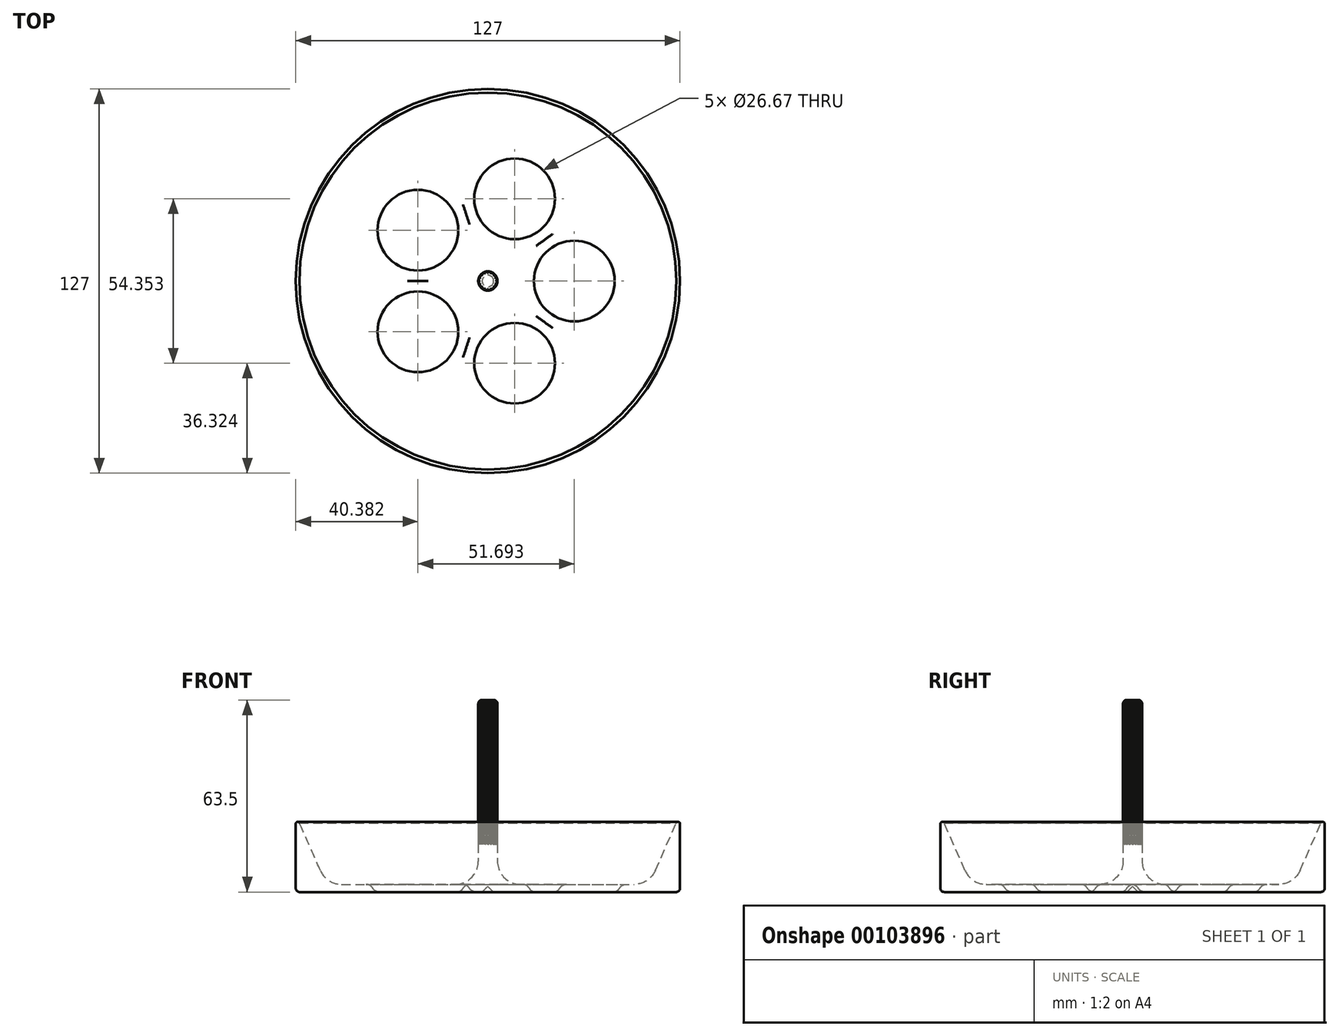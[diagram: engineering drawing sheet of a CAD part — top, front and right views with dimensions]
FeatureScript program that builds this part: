
annotation { "Feature Type Name" : "Feature", "Feature Type Description" : "" }
export const myFeature = defineFeature(function(context is Context, id is Id, definition is map)
    precondition{}
    {
        {
            var Q0;
            Q0=qCreatedBy(makeId("Front.planeOp"),FACE);
            var sketch = newSketch(context, id + "F0", { "sketchPlane" : qUnion([Q0])});
            skLineSegment(sketch, "E0", {"start": v(0, 0) * mm, "end": v(0, 63.5) * mm});
            skLineSegment(sketch, "E1", {"start": v(0, 63.5) * mm, "end": v(1.9, 63.5) * mm});
            skLineSegment(sketch, "E2", {"start": v(63.5, 22.56) * mm, "end": v(63.5, 1.27) * mm});
            skLineSegment(sketch, "E3", {"start": v(1.9, 0) * mm, "end": v(0, 1.9) * mm});
            skPoint(sketch, "E4.visualSharp", {"position": v(3.18, 2.54) * mm});
            skPoint(sketch, "E5.visualSharp", {"position": v(53.34, 2.54) * mm});
            skPoint(sketch, "E6.visualSharp", {"position": v(63.5, 25.4) * mm});
            skArc(sketch, "E6.filletArc", {"start": v(63.5, 22.56) * mm, "mid": v(63, 23.18) * mm, "end": v(62.3, 22.83) * mm});
            skPoint(sketch, "E7", {"position": v(16.72, 2.54) * mm});
            skArc(sketch, "E8", {"start": v(13.62, 1.29) * mm, "mid": v(14.28, 0.54) * mm, "end": v(15.18, 0.1) * mm});
            skArc(sketch, "E9", {"start": v(41.97, 0.1) * mm, "mid": v(42.87, 0.54) * mm, "end": v(43.53, 1.29) * mm});
            skLineSegment(sketch, "E10", {"start": v(62.3, 22.83) * mm, "end": v(55.34, 7.08) * mm});
            skLineSegment(sketch, "E11", {"start": v(3.17, 10.16) * mm, "end": v(3.17, 62.23) * mm});
            skLineSegment(sketch, "E12", {"start": v(10.8, 2.54) * mm, "end": v(11.43, 2.54) * mm});
            skLineSegment(sketch, "E13", {"start": v(45.72, 2.54) * mm, "end": v(48.37, 2.54) * mm});
            skPoint(sketch, "E14.visualSharp", {"position": v(43.9, 2.54) * mm});
            skArc(sketch, "E14.filletArc", {"start": v(45.72, 2.54) * mm, "mid": v(44.46, 2.2) * mm, "end": v(43.53, 1.29) * mm});
            skPoint(sketch, "E15.visualSharp", {"position": v(13.26, 2.54) * mm});
            skArc(sketch, "E15.filletArc", {"start": v(13.62, 1.29) * mm, "mid": v(12.7, 2.2) * mm, "end": v(11.43, 2.54) * mm});
            skLineSegment(sketch, "E16", {"start": v(11.43, 2.54) * mm, "end": v(45.72, 2.54) * mm});
            skLineSegment(sketch, "E17", {"start": v(1.9, 0) * mm, "end": v(15.88, 0) * mm});
            skLineSegment(sketch, "E18", {"start": v(15.88, 0) * mm, "end": v(41.28, 0) * mm});
            skLineSegment(sketch, "E19", {"start": v(41.28, 0) * mm, "end": v(62.23, 0) * mm});
            skLineSegment(sketch, "E20", {"start": v(28.58, 0) * mm, "end": v(28.57, 10.96) * mm});
            skArc(sketch, "E21.filletArc", {"start": v(3.17, 10.16) * mm, "mid": v(5.4, 4.77) * mm, "end": v(10.8, 2.54) * mm});
            skArc(sketch, "E22.filletArc", {"start": v(48.37, 2.54) * mm, "mid": v(52.53, 3.78) * mm, "end": v(55.34, 7.08) * mm});
            skPoint(sketch, "E23.visualSharp", {"position": v(3.17, 63.5) * mm});
            skArc(sketch, "E23.filletArc", {"start": v(3.17, 62.23) * mm, "mid": v(2.8, 63.13) * mm, "end": v(1.9, 63.5) * mm});
            skPoint(sketch, "E24.visualSharp", {"position": v(63.5, 0) * mm});
            skArc(sketch, "E24.filletArc", {"start": v(62.23, 0) * mm, "mid": v(63.13, 0.37) * mm, "end": v(63.5, 1.27) * mm});
            skLineSegment(sketch, "E25", {"start": v(15.24, 0) * mm, "end": v(15.24, 0.01) * mm});
            skLineSegment(sketch, "E26.MirrorCS", {"start": v(41.91, 0) * mm, "end": v(41.91, 0.01) * mm});
            skLineSegment(sketch, "E27.trimOffspring", {"start": v(15.24, 2.54) * mm, "end": v(15.24, 3.63) * mm});
            skLineSegment(sketch, "E28.trimOffspring", {"start": v(41.91, 2.54) * mm, "end": v(41.91, 3.63) * mm});
            skPoint(sketch, "E29.visualSharp", {"position": v(41.91, 0.08) * mm});
            skArc(sketch, "E29.filletArc", {"start": v(41.97, 0.1) * mm, "mid": v(41.93, 0.06) * mm, "end": v(41.91, 0.01) * mm});
            skPoint(sketch, "E30.visualSharp", {"position": v(15.24, 0.08) * mm});
            skArc(sketch, "E30.filletArc", {"start": v(15.24, 0.01) * mm, "mid": v(15.22, 0.06) * mm, "end": v(15.18, 0.1) * mm});
            skSolve(sketch);
        }
        {
            var Q0;
            {var subQ1=sQuery(id+"F0.wireOp",EDGE,"E1");Q0=makeQuery(id+"F0.imprint","IMPRINT",FACE,{"disambiguationData":[TD([[makeQuery(id+"F0.imprint","IMPRINT",EDGE,{"derivedFrom":subQ1}),-1.0]])]});}
            var Q1;
            {var subQ1=sQuery(id+"F0.wireOp",EDGE,"E8");Q1=makeQuery(id+"F0.imprint","IMPRINT",FACE,{"disambiguationData":[TD([[makeQuery(id+"F0.imprint","IMPRINT",EDGE,{"derivedFrom":subQ1}),1.0]])]});}
            var Q2;
            {var subQ1=sQuery(id+"F0.wireOp",EDGE,"E9");Q2=makeQuery(id+"F0.imprint","IMPRINT",FACE,{"disambiguationData":[TD([[makeQuery(id+"F0.imprint","IMPRINT",EDGE,{"derivedFrom":subQ1}),1.0]])]});}
            var Q3;
            Q3=makeQuery(id+"F0.imprint","IMPRINT",FACE,{"disambiguationData":[TD([[makeQuery(id+"F0.imprint","IMPRINT",EDGE,{"derivedFrom":sQuery(id+"F0.wireOp",EDGE,"E2")}),-1.0]])]});
            var Q4;
            Q4=sQuery(id+"F0.wireOp",EDGE,"E0");
            revolve(context, id + "F1", {"entities" : qUnion([Q0, Q1, Q2, Q3]), "axis" : qUnion([Q4]), "revolveType" : RevolveType.FULL});
        }
        {
            var Q0;
            {var subQ1=sQuery(id+"F0.wireOp",EDGE,"E8");Q0=makeQuery(id+"F0.imprint","IMPRINT",FACE,{"disambiguationData":[TD([[makeQuery(id+"F0.imprint","IMPRINT",EDGE,{"derivedFrom":subQ1}),1.0]])]});}
            var Q1;
            Q1=sQuery(id+"F0.wireOp",EDGE,"E20");
            revolve(context, id + "F2", {"entities" : qUnion([Q0]), "axis" : qUnion([Q1]), "revolveType" : RevolveType.FULL});
        }
        {
            var Q0;
            Q0=makeQuery(id+"F2.opRevolve","SWEPT_BODY",BODY,{"disambiguationData":[OSD([sQuery(id+"F0.wireOp",EDGE,"E8"),sQuery(id+"F0.wireOp",EDGE,"E15.filletArc"),sQuery(id+"F0.wireOp",EDGE,"E16"),sQuery(id+"F0.wireOp",EDGE,"E18"),sQuery(id+"F0.wireOp",EDGE,"E20")])]});
            var Q1;
            Q1=sQuery(id+"F0.wireOp",EDGE,"E0");
            circularPattern(context, id + "F3", {"entities" : qUnion([Q0]), "axis" : qUnion([Q1]), "angle" : 360 * degree, "instanceCount" : 5, "equalSpace" : true});
        }
        {
            var Q0;
            Q0=makeQuery(id+"F2.opRevolve","SWEPT_BODY",BODY,{"disambiguationData":[OSD([sQuery(id+"F0.wireOp",EDGE,"E8"),sQuery(id+"F0.wireOp",EDGE,"E15.filletArc"),sQuery(id+"F0.wireOp",EDGE,"E16"),sQuery(id+"F0.wireOp",EDGE,"E18"),sQuery(id+"F0.wireOp",EDGE,"E20")])]});
            var Q1;
            Q1=makeQuery(id+"F3.opPattern","COPY",BODY,{"derivedFrom":makeQuery(id+"F2.opRevolve","SWEPT_BODY",BODY,{"disambiguationData":[OSD([sQuery(id+"F0.wireOp",EDGE,"E8"),sQuery(id+"F0.wireOp",EDGE,"E15.filletArc"),sQuery(id+"F0.wireOp",EDGE,"E16"),sQuery(id+"F0.wireOp",EDGE,"E18"),sQuery(id+"F0.wireOp",EDGE,"E20")])]}),"instanceName":"1"});
            var Q2;
            Q2=makeQuery(id+"F3.opPattern","COPY",BODY,{"derivedFrom":makeQuery(id+"F2.opRevolve","SWEPT_BODY",BODY,{"disambiguationData":[OSD([sQuery(id+"F0.wireOp",EDGE,"E8"),sQuery(id+"F0.wireOp",EDGE,"E15.filletArc"),sQuery(id+"F0.wireOp",EDGE,"E16"),sQuery(id+"F0.wireOp",EDGE,"E18"),sQuery(id+"F0.wireOp",EDGE,"E20")])]}),"instanceName":"2"});
            var Q3;
            Q3=makeQuery(id+"F3.opPattern","COPY",BODY,{"derivedFrom":makeQuery(id+"F2.opRevolve","SWEPT_BODY",BODY,{"disambiguationData":[OSD([sQuery(id+"F0.wireOp",EDGE,"E8"),sQuery(id+"F0.wireOp",EDGE,"E15.filletArc"),sQuery(id+"F0.wireOp",EDGE,"E16"),sQuery(id+"F0.wireOp",EDGE,"E18"),sQuery(id+"F0.wireOp",EDGE,"E20")])]}),"instanceName":"3"});
            var Q4;
            Q4=makeQuery(id+"F3.opPattern","COPY",BODY,{"derivedFrom":makeQuery(id+"F2.opRevolve","SWEPT_BODY",BODY,{"disambiguationData":[OSD([sQuery(id+"F0.wireOp",EDGE,"E8"),sQuery(id+"F0.wireOp",EDGE,"E15.filletArc"),sQuery(id+"F0.wireOp",EDGE,"E16"),sQuery(id+"F0.wireOp",EDGE,"E18"),sQuery(id+"F0.wireOp",EDGE,"E20")])]}),"instanceName":"4"});
            var Q5;
            Q5=makeQuery(id+"F1.opRevolve","SWEPT_BODY",BODY,{"disambiguationData":[OSD([sQuery(id+"F0.wireOp",EDGE,"E0"),sQuery(id+"F0.wireOp",EDGE,"E1"),sQuery(id+"F0.wireOp",EDGE,"E2"),sQuery(id+"F0.wireOp",EDGE,"E3"),sQuery(id+"F0.wireOp",EDGE,"E6.filletArc"),sQuery(id+"F0.wireOp",EDGE,"E10"),sQuery(id+"F0.wireOp",EDGE,"E11"),sQuery(id+"F0.wireOp",EDGE,"E12"),sQuery(id+"F0.wireOp",EDGE,"E13"),sQuery(id+"F0.wireOp",EDGE,"E16"),sQuery(id+"F0.wireOp",EDGE,"E17"),sQuery(id+"F0.wireOp",EDGE,"E18"),sQuery(id+"F0.wireOp",EDGE,"E19"),sQuery(id+"F0.wireOp",EDGE,"E21.filletArc"),sQuery(id+"F0.wireOp",EDGE,"E22.filletArc")])]});
            booleanBodies(context, id + "F4", {"operationType" : BooleanOperationType.SUBTRACTION, "tools" : qUnion([Q0, Q1, Q2, Q3, Q4]), "targets" : qUnion([Q5])});
        }
        {
            var Q0;
            Q0=qCreatedBy(makeId("Top.planeOp"),FACE);
            var sketch = newSketch(context, id + "F5", { "sketchPlane" : qUnion([Q0])});
            skCircle(sketch, "E31", {"center": v(0, 0) * mm, "radius": 3.18 * mm});
            skLineSegment(sketch, "E32", {"start": v(0, 2.66) * mm, "end": v(0.3, 3.16) * mm});
            skLineSegment(sketch, "E33.MirrorCS", {"start": v(0, 2.66) * mm, "end": v(-0.3, 3.16) * mm});
            skLineSegment(sketch, "E34.1.0", {"start": v(-0.82, 2.53) * mm, "end": v(-0.68, 3.1) * mm});
            skLineSegment(sketch, "E34.1.1", {"start": v(-0.82, 2.53) * mm, "end": v(-1.27, 2.9) * mm});
            skLineSegment(sketch, "E34.2.0", {"start": v(-1.57, 2.16) * mm, "end": v(-1.6, 2.74) * mm});
            skLineSegment(sketch, "E34.2.1", {"start": v(-1.57, 2.16) * mm, "end": v(-2.1, 2.37) * mm});
            skLineSegment(sketch, "E34.3.0", {"start": v(-2.16, 1.57) * mm, "end": v(-2.37, 2.1) * mm});
            skLineSegment(sketch, "E34.3.1", {"start": v(-2.16, 1.57) * mm, "end": v(-2.74, 1.6) * mm});
            skLineSegment(sketch, "E34.4.0", {"start": v(-2.53, 0.82) * mm, "end": v(-2.9, 1.27) * mm});
            skLineSegment(sketch, "E34.4.1", {"start": v(-2.53, 0.82) * mm, "end": v(-3.1, 0.68) * mm});
            skLineSegment(sketch, "E34.5.0", {"start": v(-2.66, 0) * mm, "end": v(-3.16, 0.3) * mm});
            skLineSegment(sketch, "E34.5.1", {"start": v(-2.66, 0) * mm, "end": v(-3.16, -0.3) * mm});
            skLineSegment(sketch, "E34.6.0", {"start": v(-2.53, -0.82) * mm, "end": v(-3.1, -0.68) * mm});
            skLineSegment(sketch, "E34.6.1", {"start": v(-2.53, -0.82) * mm, "end": v(-2.9, -1.27) * mm});
            skLineSegment(sketch, "E34.7.0", {"start": v(-2.16, -1.57) * mm, "end": v(-2.74, -1.6) * mm});
            skLineSegment(sketch, "E34.7.1", {"start": v(-2.16, -1.57) * mm, "end": v(-2.37, -2.1) * mm});
            skLineSegment(sketch, "E34.8.0", {"start": v(-1.57, -2.16) * mm, "end": v(-2.1, -2.37) * mm});
            skLineSegment(sketch, "E34.8.1", {"start": v(-1.57, -2.16) * mm, "end": v(-1.6, -2.74) * mm});
            skLineSegment(sketch, "E34.9.0", {"start": v(-0.82, -2.53) * mm, "end": v(-1.27, -2.9) * mm});
            skLineSegment(sketch, "E34.9.1", {"start": v(-0.82, -2.53) * mm, "end": v(-0.68, -3.1) * mm});
            skLineSegment(sketch, "E34.10.0", {"start": v(0, -2.66) * mm, "end": v(-0.3, -3.16) * mm});
            skLineSegment(sketch, "E34.10.1", {"start": v(0, -2.66) * mm, "end": v(0.3, -3.16) * mm});
            skLineSegment(sketch, "E34.11.0", {"start": v(0.82, -2.53) * mm, "end": v(0.68, -3.1) * mm});
            skLineSegment(sketch, "E34.11.1", {"start": v(0.82, -2.53) * mm, "end": v(1.27, -2.9) * mm});
            skLineSegment(sketch, "E34.12.0", {"start": v(1.57, -2.16) * mm, "end": v(1.6, -2.74) * mm});
            skLineSegment(sketch, "E34.12.1", {"start": v(1.57, -2.16) * mm, "end": v(2.1, -2.37) * mm});
            skLineSegment(sketch, "E34.13.0", {"start": v(2.16, -1.57) * mm, "end": v(2.37, -2.1) * mm});
            skLineSegment(sketch, "E34.13.1", {"start": v(2.16, -1.57) * mm, "end": v(2.74, -1.6) * mm});
            skLineSegment(sketch, "E34.14.0", {"start": v(2.53, -0.82) * mm, "end": v(2.9, -1.27) * mm});
            skLineSegment(sketch, "E34.14.1", {"start": v(2.53, -0.82) * mm, "end": v(3.1, -0.68) * mm});
            skLineSegment(sketch, "E34.15.0", {"start": v(2.66, 0) * mm, "end": v(3.16, -0.3) * mm});
            skLineSegment(sketch, "E34.15.1", {"start": v(2.66, 0) * mm, "end": v(3.16, 0.3) * mm});
            skLineSegment(sketch, "E34.16.0", {"start": v(2.53, 0.82) * mm, "end": v(3.1, 0.68) * mm});
            skLineSegment(sketch, "E34.16.1", {"start": v(2.53, 0.82) * mm, "end": v(2.9, 1.27) * mm});
            skLineSegment(sketch, "E34.17.0", {"start": v(2.16, 1.57) * mm, "end": v(2.74, 1.6) * mm});
            skLineSegment(sketch, "E34.17.1", {"start": v(2.16, 1.57) * mm, "end": v(2.37, 2.1) * mm});
            skLineSegment(sketch, "E34.18.0", {"start": v(1.57, 2.16) * mm, "end": v(2.1, 2.37) * mm});
            skLineSegment(sketch, "E34.18.1", {"start": v(1.57, 2.16) * mm, "end": v(1.6, 2.74) * mm});
            skLineSegment(sketch, "E34.19.0", {"start": v(0.82, 2.53) * mm, "end": v(1.27, 2.9) * mm});
            skLineSegment(sketch, "E34.19.1", {"start": v(0.82, 2.53) * mm, "end": v(0.68, 3.1) * mm});
            skSolve(sketch);
        }
        {
            var Q0;
            {var subQ0=sQuery(id+"F5.wireOp",EDGE,"E34.3.0");Q0=makeQuery(id+"F5.imprint","IMPRINT",FACE,{"disambiguationData":[TD([[makeQuery(id+"F5.imprint","IMPRINT",EDGE,{"derivedFrom":subQ0}),1.0]])]});}
            var Q1;
            {var subQ0=sQuery(id+"F5.wireOp",EDGE,"E34.4.0");Q1=makeQuery(id+"F5.imprint","IMPRINT",FACE,{"disambiguationData":[TD([[makeQuery(id+"F5.imprint","IMPRINT",EDGE,{"derivedFrom":subQ0}),1.0]])]});}
            var Q2;
            {var subQ0=sQuery(id+"F5.wireOp",EDGE,"E34.5.0");Q2=makeQuery(id+"F5.imprint","IMPRINT",FACE,{"disambiguationData":[TD([[makeQuery(id+"F5.imprint","IMPRINT",EDGE,{"derivedFrom":subQ0}),1.0]])]});}
            var Q3;
            {var subQ0=sQuery(id+"F5.wireOp",EDGE,"E34.6.0");Q3=makeQuery(id+"F5.imprint","IMPRINT",FACE,{"disambiguationData":[TD([[makeQuery(id+"F5.imprint","IMPRINT",EDGE,{"derivedFrom":subQ0}),1.0]])]});}
            var Q4;
            {var subQ0=sQuery(id+"F5.wireOp",EDGE,"E34.7.0");Q4=makeQuery(id+"F5.imprint","IMPRINT",FACE,{"disambiguationData":[TD([[makeQuery(id+"F5.imprint","IMPRINT",EDGE,{"derivedFrom":subQ0}),1.0]])]});}
            var Q5;
            {var subQ0=sQuery(id+"F5.wireOp",EDGE,"E34.8.0");Q5=makeQuery(id+"F5.imprint","IMPRINT",FACE,{"disambiguationData":[TD([[makeQuery(id+"F5.imprint","IMPRINT",EDGE,{"derivedFrom":subQ0}),1.0]])]});}
            var Q6;
            {var subQ0=sQuery(id+"F5.wireOp",EDGE,"E34.9.0");Q6=makeQuery(id+"F5.imprint","IMPRINT",FACE,{"disambiguationData":[TD([[makeQuery(id+"F5.imprint","IMPRINT",EDGE,{"derivedFrom":subQ0}),1.0]])]});}
            var Q7;
            {var subQ0=sQuery(id+"F5.wireOp",EDGE,"E34.10.0");Q7=makeQuery(id+"F5.imprint","IMPRINT",FACE,{"disambiguationData":[TD([[makeQuery(id+"F5.imprint","IMPRINT",EDGE,{"derivedFrom":subQ0}),1.0]])]});}
            var Q8;
            {var subQ0=sQuery(id+"F5.wireOp",EDGE,"E34.11.0");Q8=makeQuery(id+"F5.imprint","IMPRINT",FACE,{"disambiguationData":[TD([[makeQuery(id+"F5.imprint","IMPRINT",EDGE,{"derivedFrom":subQ0}),1.0]])]});}
            var Q9;
            {var subQ0=sQuery(id+"F5.wireOp",EDGE,"E34.12.0");Q9=makeQuery(id+"F5.imprint","IMPRINT",FACE,{"disambiguationData":[TD([[makeQuery(id+"F5.imprint","IMPRINT",EDGE,{"derivedFrom":subQ0}),1.0]])]});}
            var Q10;
            {var subQ0=sQuery(id+"F5.wireOp",EDGE,"E34.13.0");Q10=makeQuery(id+"F5.imprint","IMPRINT",FACE,{"disambiguationData":[TD([[makeQuery(id+"F5.imprint","IMPRINT",EDGE,{"derivedFrom":subQ0}),1.0]])]});}
            var Q11;
            {var subQ0=sQuery(id+"F5.wireOp",EDGE,"E34.14.0");Q11=makeQuery(id+"F5.imprint","IMPRINT",FACE,{"disambiguationData":[TD([[makeQuery(id+"F5.imprint","IMPRINT",EDGE,{"derivedFrom":subQ0}),1.0]])]});}
            var Q12;
            {var subQ0=sQuery(id+"F5.wireOp",EDGE,"E34.15.0");Q12=makeQuery(id+"F5.imprint","IMPRINT",FACE,{"disambiguationData":[TD([[makeQuery(id+"F5.imprint","IMPRINT",EDGE,{"derivedFrom":subQ0}),1.0]])]});}
            var Q13;
            {var subQ0=sQuery(id+"F5.wireOp",EDGE,"E34.16.0");Q13=makeQuery(id+"F5.imprint","IMPRINT",FACE,{"disambiguationData":[TD([[makeQuery(id+"F5.imprint","IMPRINT",EDGE,{"derivedFrom":subQ0}),1.0]])]});}
            var Q14;
            {var subQ0=sQuery(id+"F5.wireOp",EDGE,"E34.17.0");Q14=makeQuery(id+"F5.imprint","IMPRINT",FACE,{"disambiguationData":[TD([[makeQuery(id+"F5.imprint","IMPRINT",EDGE,{"derivedFrom":subQ0}),1.0]])]});}
            var Q15;
            {var subQ0=sQuery(id+"F5.wireOp",EDGE,"E34.18.0");Q15=makeQuery(id+"F5.imprint","IMPRINT",FACE,{"disambiguationData":[TD([[makeQuery(id+"F5.imprint","IMPRINT",EDGE,{"derivedFrom":subQ0}),1.0]])]});}
            var Q16;
            {var subQ0=sQuery(id+"F5.wireOp",EDGE,"E34.19.0");Q16=makeQuery(id+"F5.imprint","IMPRINT",FACE,{"disambiguationData":[TD([[makeQuery(id+"F5.imprint","IMPRINT",EDGE,{"derivedFrom":subQ0}),1.0]])]});}
            var Q17;
            {var subQ0=sQuery(id+"F5.wireOp",EDGE,"E32");Q17=makeQuery(id+"F5.imprint","IMPRINT",FACE,{"disambiguationData":[TD([[makeQuery(id+"F5.imprint","IMPRINT",EDGE,{"derivedFrom":subQ0}),1.0]])]});}
            var Q18;
            {var subQ0=sQuery(id+"F5.wireOp",EDGE,"E34.1.0");Q18=makeQuery(id+"F5.imprint","IMPRINT",FACE,{"disambiguationData":[TD([[makeQuery(id+"F5.imprint","IMPRINT",EDGE,{"derivedFrom":subQ0}),1.0]])]});}
            var Q19;
            {var subQ0=sQuery(id+"F5.wireOp",EDGE,"E34.2.0");Q19=makeQuery(id+"F5.imprint","IMPRINT",FACE,{"disambiguationData":[TD([[makeQuery(id+"F5.imprint","IMPRINT",EDGE,{"derivedFrom":subQ0}),1.0]])]});}
            extrude(context, id + "F6", {"entities" : qUnion([Q0, Q1, Q2, Q3, Q4, Q5, Q6, Q7, Q8, Q9, Q10, Q11, Q12, Q13, Q14, Q15, Q16, Q17, Q18, Q19]), "depth" : 65.53 * mm, "hasSecondDirection" : true, "secondDirectionOppositeDirection" : false, "secondDirectionDepth" : 15.88 * mm});
        }
        {
            var Q0;
            Q0=makeQuery(id+"F6.opExtrude","SWEPT_BODY",BODY,{"disambiguationData":[OSD([sQuery(id+"F5.wireOp",EDGE,"E31"),sQuery(id+"F5.wireOp",EDGE,"E34.16.0"),sQuery(id+"F5.wireOp",EDGE,"E34.16.1")])]});
            var Q1;
            Q1=makeQuery(id+"F6.opExtrude","SWEPT_BODY",BODY,{"disambiguationData":[OSD([sQuery(id+"F5.wireOp",EDGE,"E31"),sQuery(id+"F5.wireOp",EDGE,"E34.17.0"),sQuery(id+"F5.wireOp",EDGE,"E34.17.1")])]});
            var Q2;
            Q2=makeQuery(id+"F6.opExtrude","SWEPT_BODY",BODY,{"disambiguationData":[OSD([sQuery(id+"F5.wireOp",EDGE,"E31"),sQuery(id+"F5.wireOp",EDGE,"E34.18.0"),sQuery(id+"F5.wireOp",EDGE,"E34.18.1")])]});
            var Q3;
            Q3=makeQuery(id+"F6.opExtrude","SWEPT_BODY",BODY,{"disambiguationData":[OSD([sQuery(id+"F5.wireOp",EDGE,"E31"),sQuery(id+"F5.wireOp",EDGE,"E34.19.0"),sQuery(id+"F5.wireOp",EDGE,"E34.19.1")])]});
            var Q4;
            Q4=makeQuery(id+"F6.opExtrude","SWEPT_BODY",BODY,{"disambiguationData":[OSD([sQuery(id+"F5.wireOp",EDGE,"E31"),sQuery(id+"F5.wireOp",EDGE,"E32"),sQuery(id+"F5.wireOp",EDGE,"E33.MirrorCS")])]});
            var Q5;
            Q5=makeQuery(id+"F6.opExtrude","SWEPT_BODY",BODY,{"disambiguationData":[OSD([sQuery(id+"F5.wireOp",EDGE,"E31"),sQuery(id+"F5.wireOp",EDGE,"E34.1.0"),sQuery(id+"F5.wireOp",EDGE,"E34.1.1")])]});
            var Q6;
            Q6=makeQuery(id+"F6.opExtrude","SWEPT_BODY",BODY,{"disambiguationData":[OSD([sQuery(id+"F5.wireOp",EDGE,"E31"),sQuery(id+"F5.wireOp",EDGE,"E34.2.0"),sQuery(id+"F5.wireOp",EDGE,"E34.2.1")])]});
            var Q7;
            Q7=makeQuery(id+"F6.opExtrude","SWEPT_BODY",BODY,{"disambiguationData":[OSD([sQuery(id+"F5.wireOp",EDGE,"E31"),sQuery(id+"F5.wireOp",EDGE,"E34.3.0"),sQuery(id+"F5.wireOp",EDGE,"E34.3.1")])]});
            var Q8;
            Q8=makeQuery(id+"F6.opExtrude","SWEPT_BODY",BODY,{"disambiguationData":[OSD([sQuery(id+"F5.wireOp",EDGE,"E31"),sQuery(id+"F5.wireOp",EDGE,"E34.4.0"),sQuery(id+"F5.wireOp",EDGE,"E34.4.1")])]});
            var Q9;
            Q9=makeQuery(id+"F6.opExtrude","SWEPT_BODY",BODY,{"disambiguationData":[OSD([sQuery(id+"F5.wireOp",EDGE,"E31"),sQuery(id+"F5.wireOp",EDGE,"E34.5.0"),sQuery(id+"F5.wireOp",EDGE,"E34.5.1")])]});
            var Q10;
            Q10=makeQuery(id+"F6.opExtrude","SWEPT_BODY",BODY,{"disambiguationData":[OSD([sQuery(id+"F5.wireOp",EDGE,"E31"),sQuery(id+"F5.wireOp",EDGE,"E34.6.0"),sQuery(id+"F5.wireOp",EDGE,"E34.6.1")])]});
            var Q11;
            Q11=makeQuery(id+"F6.opExtrude","SWEPT_BODY",BODY,{"disambiguationData":[OSD([sQuery(id+"F5.wireOp",EDGE,"E31"),sQuery(id+"F5.wireOp",EDGE,"E34.7.0"),sQuery(id+"F5.wireOp",EDGE,"E34.7.1")])]});
            var Q12;
            Q12=makeQuery(id+"F6.opExtrude","SWEPT_BODY",BODY,{"disambiguationData":[OSD([sQuery(id+"F5.wireOp",EDGE,"E31"),sQuery(id+"F5.wireOp",EDGE,"E34.8.0"),sQuery(id+"F5.wireOp",EDGE,"E34.8.1")])]});
            var Q13;
            Q13=makeQuery(id+"F6.opExtrude","SWEPT_BODY",BODY,{"disambiguationData":[OSD([sQuery(id+"F5.wireOp",EDGE,"E31"),sQuery(id+"F5.wireOp",EDGE,"E34.9.0"),sQuery(id+"F5.wireOp",EDGE,"E34.9.1")])]});
            var Q14;
            Q14=makeQuery(id+"F6.opExtrude","SWEPT_BODY",BODY,{"disambiguationData":[OSD([sQuery(id+"F5.wireOp",EDGE,"E31"),sQuery(id+"F5.wireOp",EDGE,"E34.10.0"),sQuery(id+"F5.wireOp",EDGE,"E34.10.1")])]});
            var Q15;
            Q15=makeQuery(id+"F6.opExtrude","SWEPT_BODY",BODY,{"disambiguationData":[OSD([sQuery(id+"F5.wireOp",EDGE,"E31"),sQuery(id+"F5.wireOp",EDGE,"E34.11.0"),sQuery(id+"F5.wireOp",EDGE,"E34.11.1")])]});
            var Q16;
            Q16=makeQuery(id+"F6.opExtrude","SWEPT_BODY",BODY,{"disambiguationData":[OSD([sQuery(id+"F5.wireOp",EDGE,"E31"),sQuery(id+"F5.wireOp",EDGE,"E34.12.0"),sQuery(id+"F5.wireOp",EDGE,"E34.12.1")])]});
            var Q17;
            Q17=makeQuery(id+"F6.opExtrude","SWEPT_BODY",BODY,{"disambiguationData":[OSD([sQuery(id+"F5.wireOp",EDGE,"E31"),sQuery(id+"F5.wireOp",EDGE,"E34.13.0"),sQuery(id+"F5.wireOp",EDGE,"E34.13.1")])]});
            var Q18;
            Q18=makeQuery(id+"F6.opExtrude","SWEPT_BODY",BODY,{"disambiguationData":[OSD([sQuery(id+"F5.wireOp",EDGE,"E31"),sQuery(id+"F5.wireOp",EDGE,"E34.14.0"),sQuery(id+"F5.wireOp",EDGE,"E34.14.1")])]});
            var Q19;
            Q19=makeQuery(id+"F6.opExtrude","SWEPT_BODY",BODY,{"disambiguationData":[OSD([sQuery(id+"F5.wireOp",EDGE,"E31"),sQuery(id+"F5.wireOp",EDGE,"E34.15.0"),sQuery(id+"F5.wireOp",EDGE,"E34.15.1")])]});
            var Q20;
            Q20=makeQuery(id+"F1.opRevolve","SWEPT_BODY",BODY,{"disambiguationData":[OSD([sQuery(id+"F0.wireOp",EDGE,"E0"),sQuery(id+"F0.wireOp",EDGE,"E1"),sQuery(id+"F0.wireOp",EDGE,"E2"),sQuery(id+"F0.wireOp",EDGE,"E3"),sQuery(id+"F0.wireOp",EDGE,"E6.filletArc"),sQuery(id+"F0.wireOp",EDGE,"E10"),sQuery(id+"F0.wireOp",EDGE,"E11"),sQuery(id+"F0.wireOp",EDGE,"E12"),sQuery(id+"F0.wireOp",EDGE,"E13"),sQuery(id+"F0.wireOp",EDGE,"E16"),sQuery(id+"F0.wireOp",EDGE,"E17"),sQuery(id+"F0.wireOp",EDGE,"E18"),sQuery(id+"F0.wireOp",EDGE,"E19"),sQuery(id+"F0.wireOp",EDGE,"E21.filletArc"),sQuery(id+"F0.wireOp",EDGE,"E22.filletArc"),sQuery(id+"F0.wireOp",EDGE,"E23.filletArc")])]});
            booleanBodies(context, id + "F7", {"operationType" : BooleanOperationType.SUBTRACTION, "tools" : qUnion([Q0, Q1, Q2, Q3, Q4, Q5, Q6, Q7, Q8, Q9, Q10, Q11, Q12, Q13, Q14, Q15, Q16, Q17, Q18, Q19]), "targets" : qUnion([Q20])});
        }
    });
